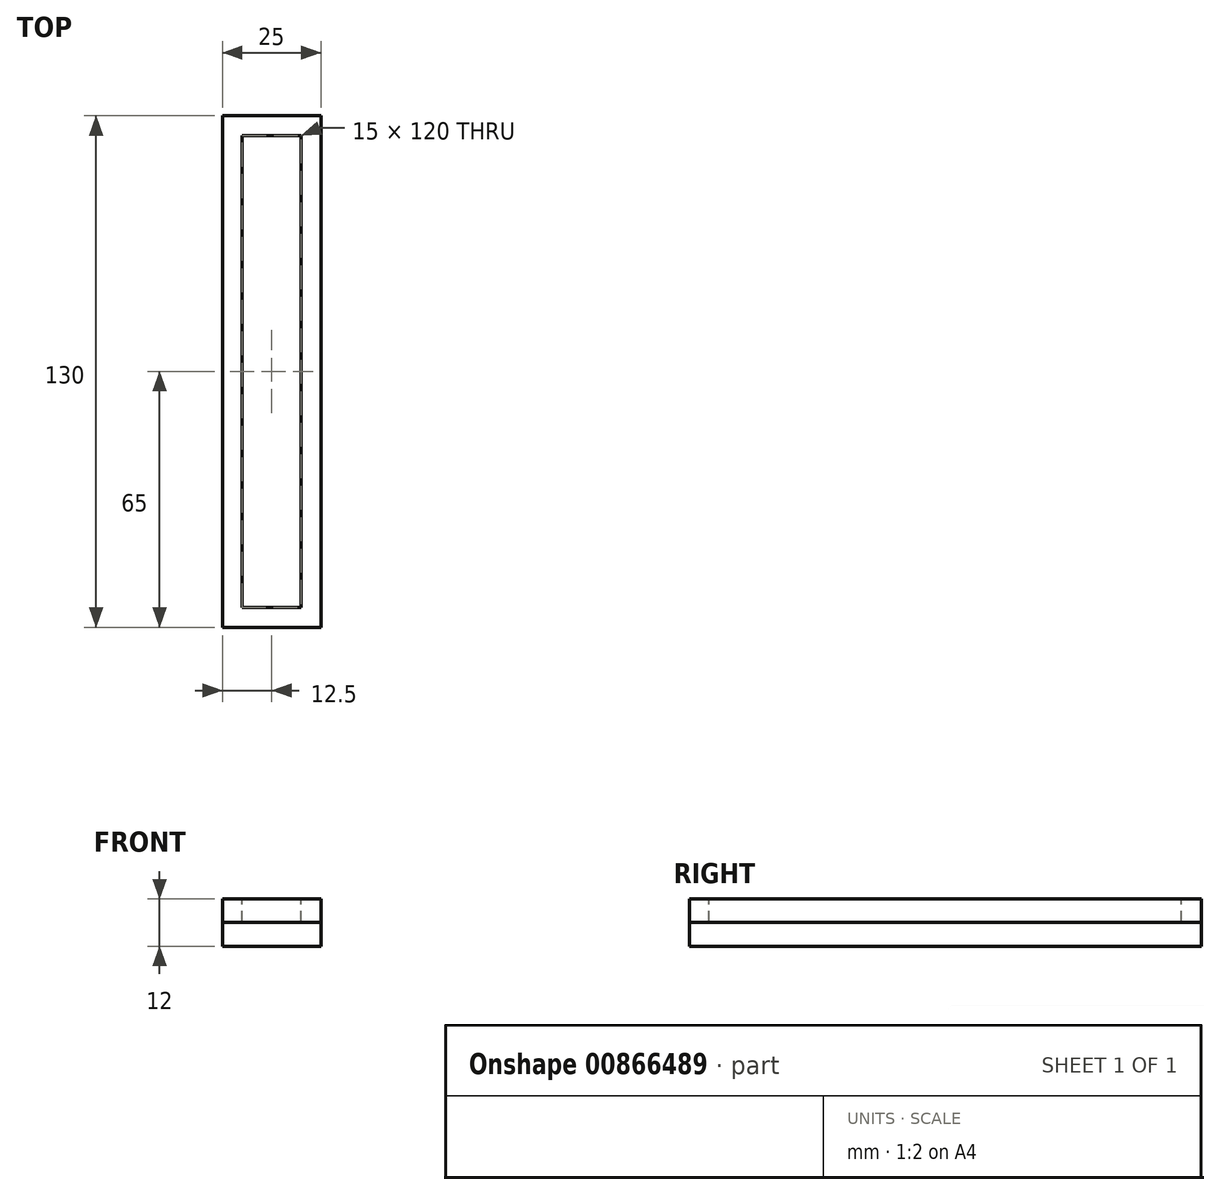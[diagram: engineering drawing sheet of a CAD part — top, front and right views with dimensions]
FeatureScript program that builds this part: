
annotation { "Feature Type Name" : "Feature", "Feature Type Description" : "" }
export const myFeature = defineFeature(function(context is Context, id is Id, definition is map)
    precondition{}
    {
        {
            var Q0;
            Q0=qCreatedBy(makeId("Top.planeOp"),FACE);
            var sketch = newSketch(context, id + "F0", { "sketchPlane" : qUnion([Q0])});
            skLineSegment(sketch, "E0.bottom", {"start": v(0, 0) * mm, "end": v(15, 0) * mm});
            skLineSegment(sketch, "E0.top", {"start": v(0, 120) * mm, "end": v(15, 120) * mm});
            skLineSegment(sketch, "E0.left", {"start": v(0, 0) * mm, "end": v(0, 120) * mm});
            skLineSegment(sketch, "E0.right", {"start": v(15, 0) * mm, "end": v(15, 120) * mm});
            skLineSegment(sketch, "E1.0", {"start": v(-5, 125) * mm, "end": v(20, 125) * mm});
            skLineSegment(sketch, "E1.1", {"start": v(-5, -5) * mm, "end": v(-5, 125) * mm});
            skLineSegment(sketch, "E1.2", {"start": v(-5, -5) * mm, "end": v(20, -5) * mm});
            skLineSegment(sketch, "E1.3", {"start": v(20, -5) * mm, "end": v(20, 125) * mm});
            skSolve(sketch);
        }
        {
            var Q0;
            Q0=makeQuery(id+"F0.imprint","IMPRINT",FACE,{"disambiguationData":[TD([[makeQuery(id+"F0.imprint","IMPRINT",EDGE,{"derivedFrom":sQuery(id+"F0.wireOp",EDGE,"E0.bottom")}),-1.0]])]});
            extrude(context, id + "F1", {"entities" : qUnion([Q0]), "oppositeDirection" : true, "depth" : 6 * mm, "offsetDistance" : 25 * mm});
        }
        {
            var Q0;
            Q0=makeQuery(id+"F1.opExtrude","CAP_FACE",FACE,{"disambiguationData":[OSD([sQuery(id+"F0.wireOp",EDGE,"E0.bottom"),sQuery(id+"F0.wireOp",EDGE,"E0.top"),sQuery(id+"F0.wireOp",EDGE,"E0.left"),sQuery(id+"F0.wireOp",EDGE,"E0.right"),sQuery(id+"F0.wireOp",EDGE,"E1.0"),sQuery(id+"F0.wireOp",EDGE,"E1.1"),sQuery(id+"F0.wireOp",EDGE,"E1.2"),sQuery(id+"F0.wireOp",EDGE,"E1.3")])],"isStart":false});
            var sketch = newSketch(context, id + "F2", { "sketchPlane" : qUnion([Q0])});
            skLineSegment(sketch, "E2.bottom", {"start": v(-5, 5) * mm, "end": v(20, 5) * mm});
            skLineSegment(sketch, "E2.top", {"start": v(-5, -125) * mm, "end": v(20, -125) * mm});
            skLineSegment(sketch, "E2.left", {"start": v(-5, 5) * mm, "end": v(-5, -125) * mm});
            skLineSegment(sketch, "E2.right", {"start": v(20, 5) * mm, "end": v(20, -125) * mm});
            skSolve(sketch);
        }
        {
            var Q0;
            Q0 = qSketchRegion(id + "F2", true);
            extrude(context, id + "F3", {"entities" : qUnion([Q0]), "depth" : 6 * mm, "offsetDistance" : 25 * mm});
        }
    });
